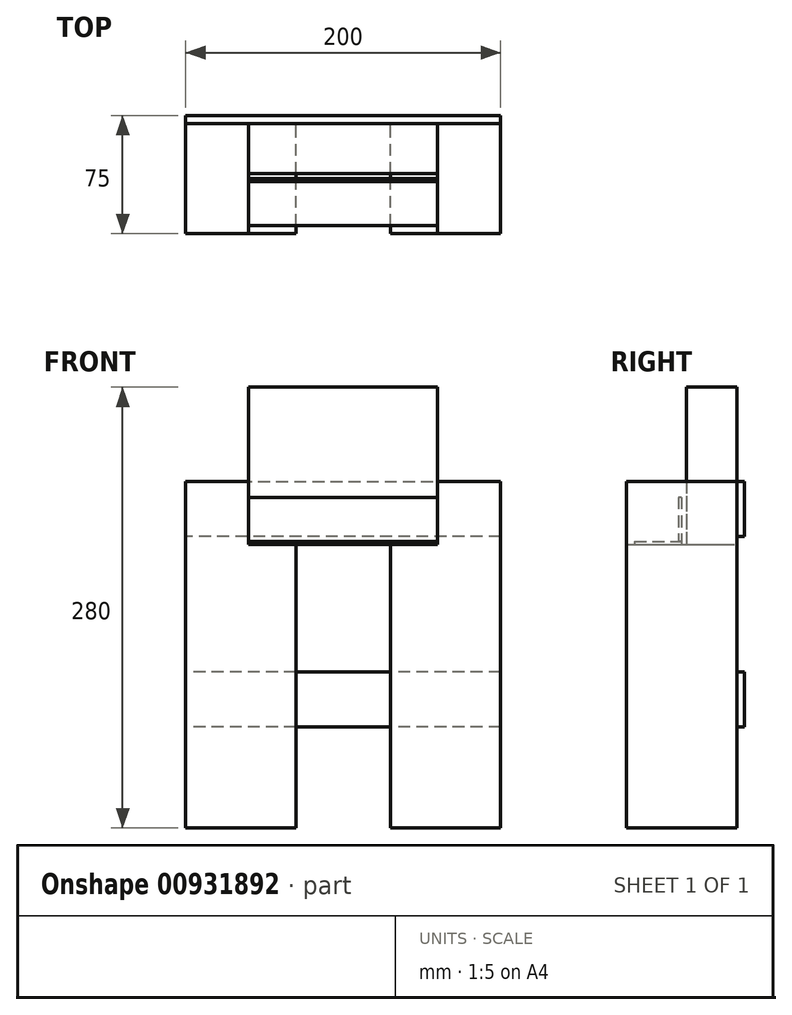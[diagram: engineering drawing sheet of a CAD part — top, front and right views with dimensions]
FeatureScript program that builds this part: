
annotation { "Feature Type Name" : "Feature", "Feature Type Description" : "" }
export const myFeature = defineFeature(function(context is Context, id is Id, definition is map)
    precondition{}
    {
        {
            var Q0;
            Q0=qCreatedBy(makeId("Top.planeOp"),FACE);
            var sketch = newSketch(context, id + "F0", { "sketchPlane" : qUnion([Q0])});
            skLineSegment(sketch, "E0.bottom", {"start": v(0, 0) * mm, "end": v(70, 0) * mm});
            skLineSegment(sketch, "E0.top", {"start": v(0, 70) * mm, "end": v(70, 70) * mm});
            skLineSegment(sketch, "E0.left", {"start": v(0, 0) * mm, "end": v(0, 70) * mm});
            skLineSegment(sketch, "E0.right", {"start": v(70, 0) * mm, "end": v(70, 70) * mm});
            skLineSegment(sketch, "E1.bottom", {"start": v(-60, 0) * mm, "end": v(-130, 0) * mm});
            skLineSegment(sketch, "E1.top", {"start": v(-60, 70) * mm, "end": v(-130, 70) * mm});
            skLineSegment(sketch, "E1.left", {"start": v(-60, 0) * mm, "end": v(-60, 70) * mm});
            skLineSegment(sketch, "E1.right", {"start": v(-130, 0) * mm, "end": v(-130, 70) * mm});
            skSolve(sketch);
        }
        {
            var Q0;
            Q0=makeQuery(id+"F0.imprint","IMPRINT",FACE,{"disambiguationData":[TD([[makeQuery(id+"F0.imprint","IMPRINT",EDGE,{"derivedFrom":sQuery(id+"F0.wireOp",EDGE,"E1.bottom")}),-1.0]])]});
            var Q1;
            Q1=makeQuery(id+"F0.imprint","IMPRINT",FACE,{"disambiguationData":[TD([[makeQuery(id+"F0.imprint","IMPRINT",EDGE,{"derivedFrom":sQuery(id+"F0.wireOp",EDGE,"E0.bottom")}),1.0]])]});
            extrude(context, id + "F1", {"entities" : qUnion([Q0, Q1]), "depth" : 220 * mm, "offsetDistance" : 25 * mm});
        }
        {
            var Q0;
            Q0=makeQuery(id+"F1.opExtrude","CAP_FACE",FACE,{"disambiguationData":[OSD([sQuery(id+"F0.wireOp",EDGE,"E1.bottom"),sQuery(id+"F0.wireOp",EDGE,"E1.top"),sQuery(id+"F0.wireOp",EDGE,"E1.left"),sQuery(id+"F0.wireOp",EDGE,"E1.right")])],"isStart":false});
            var sketch = newSketch(context, id + "F2", { "sketchPlane" : qUnion([Q0])});
            skLineSegment(sketch, "E2.bottom", {"start": v(-60, 0) * mm, "end": v(-90, 0) * mm});
            skLineSegment(sketch, "E2.top", {"start": v(-60, 70) * mm, "end": v(-90, 70) * mm});
            skLineSegment(sketch, "E2.left", {"start": v(-60, 0) * mm, "end": v(-60, 70) * mm});
            skLineSegment(sketch, "E2.right", {"start": v(-90, 0) * mm, "end": v(-90, 70) * mm});
            skSolve(sketch);
        }
        {
            var Q0;
            Q0=makeQuery(id+"F1.opExtrude","CAP_FACE",FACE,{"disambiguationData":[OSD([sQuery(id+"F0.wireOp",EDGE,"E0.bottom"),sQuery(id+"F0.wireOp",EDGE,"E0.top"),sQuery(id+"F0.wireOp",EDGE,"E0.left"),sQuery(id+"F0.wireOp",EDGE,"E0.right")])],"isStart":false});
            var sketch = newSketch(context, id + "F3", { "sketchPlane" : qUnion([Q0])});
            skLineSegment(sketch, "E3.bottom", {"start": v(0, 0) * mm, "end": v(30, 0) * mm});
            skLineSegment(sketch, "E3.top", {"start": v(0, 70) * mm, "end": v(30, 70) * mm});
            skLineSegment(sketch, "E3.left", {"start": v(0, 0) * mm, "end": v(0, 70) * mm});
            skLineSegment(sketch, "E3.right", {"start": v(30, 0) * mm, "end": v(30, 70) * mm});
            skSolve(sketch);
        }
        {
            var Q0;
            Q0=makeQuery(id+"F2.imprint","IMPRINT",FACE,{"disambiguationData":[TD([[makeQuery(id+"F2.imprint","IMPRINT",EDGE,{"derivedFrom":sQuery(id+"F2.wireOp",EDGE,"E2.bottom")}),-1.0]])]});
            extrude(context, id + "F4", {"entities" : qUnion([Q0]), "operationType" : NewBodyOperationType.REMOVE, "oppositeDirection" : true, "depth" : 40 * mm, "offsetDistance" : 25 * mm});
        }
        {
            var Q0;
            Q0=makeQuery(id+"F3.imprint","IMPRINT",FACE,{"disambiguationData":[TD([[makeQuery(id+"F3.imprint","IMPRINT",EDGE,{"derivedFrom":sQuery(id+"F3.wireOp",EDGE,"E3.bottom")}),1.0]])]});
            extrude(context, id + "F5", {"entities" : qUnion([Q0]), "operationType" : NewBodyOperationType.REMOVE, "oppositeDirection" : true, "depth" : 40 * mm, "offsetDistance" : 25 * mm});
        }
        {
            var Q0;
            Q0=makeQuery(id+"F4.boolean.opBoolean","COPY",FACE,{"derivedFrom":makeQuery(id+"F4.opExtrude","CAP_FACE",FACE,{"disambiguationData":[OSD([sQuery(id+"F2.wireOp",EDGE,"E2.bottom"),sQuery(id+"F2.wireOp",EDGE,"E2.top"),sQuery(id+"F2.wireOp",EDGE,"E2.left"),sQuery(id+"F2.wireOp",EDGE,"E2.right")])],"isStart":false})});
            var sketch = newSketch(context, id + "F6", { "sketchPlane" : qUnion([Q0])});
            skLineSegment(sketch, "E4.bottom", {"start": v(-90, 70) * mm, "end": v(30, 70) * mm});
            skLineSegment(sketch, "E4.top", {"start": v(-90, 38) * mm, "end": v(30, 38) * mm});
            skLineSegment(sketch, "E4.left", {"start": v(-90, 70) * mm, "end": v(-90, 38) * mm});
            skLineSegment(sketch, "E4.right", {"start": v(30, 70) * mm, "end": v(30, 38) * mm});
            skSolve(sketch);
        }
        {
            var Q0;
            {var subQ3=sQuery(id+"F6.wireOp",EDGE,"E4.left");Q0=makeQuery(id+"F6.imprint","IMPRINT",FACE,{"disambiguationData":[TD([[makeQuery(id+"F6.imprint","IMPRINT",EDGE,{"derivedFrom":subQ3}),-1.0]])]});}
            var Q1;
            {var subQ3=sQuery(id+"F6.wireOp",EDGE,"E4.right");Q1=makeQuery(id+"F6.imprint","IMPRINT",FACE,{"disambiguationData":[TD([[makeQuery(id+"F6.imprint","IMPRINT",EDGE,{"derivedFrom":subQ3}),-1.0]])]});}
            extrude(context, id + "F7", {"entities" : qUnion([Q0, Q1]), "depth" : 100 * mm, "offsetDistance" : 25 * mm});
        }
        {
            var Q0;
            Q0=makeQuery(id+"F1.opExtrude","SWEPT_FACE",FACE,{"disambiguationData":[OSD([sQuery(id+"F0.wireOp",EDGE,"E0.top")])]});
            var sketch = newSketch(context, id + "F8", { "sketchPlane" : qUnion([Q0])});
            skLineSegment(sketch, "E5.bottom", {"start": v(-70, 220) * mm, "end": v(130, 220) * mm});
            skLineSegment(sketch, "E5.top", {"start": v(-70, 185) * mm, "end": v(130, 185) * mm});
            skLineSegment(sketch, "E5.left", {"start": v(-70, 220) * mm, "end": v(-70, 185) * mm});
            skLineSegment(sketch, "E5.right", {"start": v(130, 220) * mm, "end": v(130, 185) * mm});
            skSolve(sketch);
        }
        {
            var Q0;
            {var subQ0=sQuery(id+"F8.wireOp",EDGE,"E5.left");Q0=makeQuery(id+"F8.imprint","IMPRINT",FACE,{"disambiguationData":[TD([[makeQuery(id+"F8.imprint","IMPRINT",EDGE,{"derivedFrom":subQ0}),1.0]])]});}
            var Q1;
            {var subQ3=sQuery(id+"F8.wireOp",EDGE,"E5.right");Q1=makeQuery(id+"F8.imprint","IMPRINT",FACE,{"disambiguationData":[TD([[makeQuery(id+"F8.imprint","IMPRINT",EDGE,{"derivedFrom":subQ3}),-1.0]])]});}
            extrude(context, id + "F9", {"entities" : qUnion([Q0, Q1]), "depth" : 5 * mm, "offsetDistance" : 25 * mm});
        }
        {
            var Q0;
            Q0=makeQuery(id+"F1.opExtrude","SWEPT_FACE",FACE,{"disambiguationData":[OSD([sQuery(id+"F0.wireOp",EDGE,"E0.top")])]});
            var sketch = newSketch(context, id + "F10", { "sketchPlane" : qUnion([Q0])});
            skLineSegment(sketch, "E6.bottom", {"start": v(-70, 64.16) * mm, "end": v(130, 64.16) * mm});
            skLineSegment(sketch, "E6.top", {"start": v(-70, 99.16) * mm, "end": v(130, 99.16) * mm});
            skLineSegment(sketch, "E6.left", {"start": v(-70, 64.16) * mm, "end": v(-70, 99.16) * mm});
            skLineSegment(sketch, "E6.right", {"start": v(130, 64.16) * mm, "end": v(130, 99.16) * mm});
            skSolve(sketch);
        }
        {
            var Q0;
            {var subQ0=sQuery(id+"F10.wireOp",EDGE,"E6.left");Q0=makeQuery(id+"F10.imprint","IMPRINT",FACE,{"disambiguationData":[TD([[makeQuery(id+"F10.imprint","IMPRINT",EDGE,{"derivedFrom":subQ0}),1.0]])]});}
            var Q1;
            {var subQ0=sQuery(id+"F10.wireOp",EDGE,"E6.right");Q1=makeQuery(id+"F10.imprint","IMPRINT",FACE,{"disambiguationData":[TD([[makeQuery(id+"F10.imprint","IMPRINT",EDGE,{"derivedFrom":subQ0}),1.0]])]});}
            extrude(context, id + "F11", {"entities" : qUnion([Q0, Q1]), "depth" : 5 * mm, "offsetDistance" : 25 * mm});
        }
        {
            var Q0;
            Q0=makeQuery(id+"F5.boolean.opBoolean","COPY",FACE,{"derivedFrom":makeQuery(id+"F5.opExtrude","CAP_FACE",FACE,{"disambiguationData":[OSD([sQuery(id+"F3.wireOp",EDGE,"E3.bottom"),sQuery(id+"F3.wireOp",EDGE,"E3.top"),sQuery(id+"F3.wireOp",EDGE,"E3.left"),sQuery(id+"F3.wireOp",EDGE,"E3.right")])],"isStart":false})});
            var sketch = newSketch(context, id + "F12", { "sketchPlane" : qUnion([Q0])});
            skLineSegment(sketch, "E7.bottom", {"start": v(30, 35) * mm, "end": v(-90, 35) * mm});
            skLineSegment(sketch, "E7.top", {"start": v(30, 5) * mm, "end": v(-90, 5) * mm});
            skLineSegment(sketch, "E7.left", {"start": v(30, 35) * mm, "end": v(30, 5) * mm});
            skLineSegment(sketch, "E7.right", {"start": v(-90, 35) * mm, "end": v(-90, 5) * mm});
            skSolve(sketch);
        }
        {
            var Q0;
            {var subQ0=sQuery(id+"F12.wireOp",EDGE,"E7.right");Q0=makeQuery(id+"F12.imprint","IMPRINT",FACE,{"disambiguationData":[TD([[makeQuery(id+"F12.imprint","IMPRINT",EDGE,{"derivedFrom":subQ0}),1.0]])]});}
            var Q1;
            {var subQ0=sQuery(id+"F12.wireOp",EDGE,"E7.left");Q1=makeQuery(id+"F12.imprint","IMPRINT",FACE,{"disambiguationData":[TD([[makeQuery(id+"F12.imprint","IMPRINT",EDGE,{"derivedFrom":subQ0}),1.0]])]});}
            extrude(context, id + "F13", {"entities" : qUnion([Q0, Q1]), "depth" : 2 * mm, "offsetDistance" : 25 * mm});
        }
        {
            var Q0;
            Q0=makeQuery(id+"F13.opExtrude","CAP_FACE",FACE,{"disambiguationData":[OSD([sQuery(id+"F12.wireOp",EDGE,"E7.bottom"),sQuery(id+"F12.wireOp",EDGE,"E7.top"),sQuery(id+"F12.wireOp",EDGE,"E7.left"),sQuery(id+"F12.wireOp",EDGE,"E7.right")])],"isStart":false});
            var sketch = newSketch(context, id + "F14", { "sketchPlane" : qUnion([Q0])});
            skLineSegment(sketch, "E8.bottom", {"start": v(-90, 35) * mm, "end": v(30, 35) * mm});
            skLineSegment(sketch, "E8.top", {"start": v(-90, 33) * mm, "end": v(30, 33) * mm});
            skLineSegment(sketch, "E8.left", {"start": v(-90, 35) * mm, "end": v(-90, 33) * mm});
            skLineSegment(sketch, "E8.right", {"start": v(30, 35) * mm, "end": v(30, 33) * mm});
            skSolve(sketch);
        }
        {
            var Q0;
            Q0=makeQuery(id+"F14.imprint","IMPRINT",FACE,{"disambiguationData":[TD([[makeQuery(id+"F14.imprint","IMPRINT",EDGE,{"derivedFrom":sQuery(id+"F14.wireOp",EDGE,"E8.bottom")}),1.0]])]});
            extrude(context, id + "F15", {"entities" : qUnion([Q0]), "depth" : 28 * mm, "offsetDistance" : 25 * mm});
        }
    });
